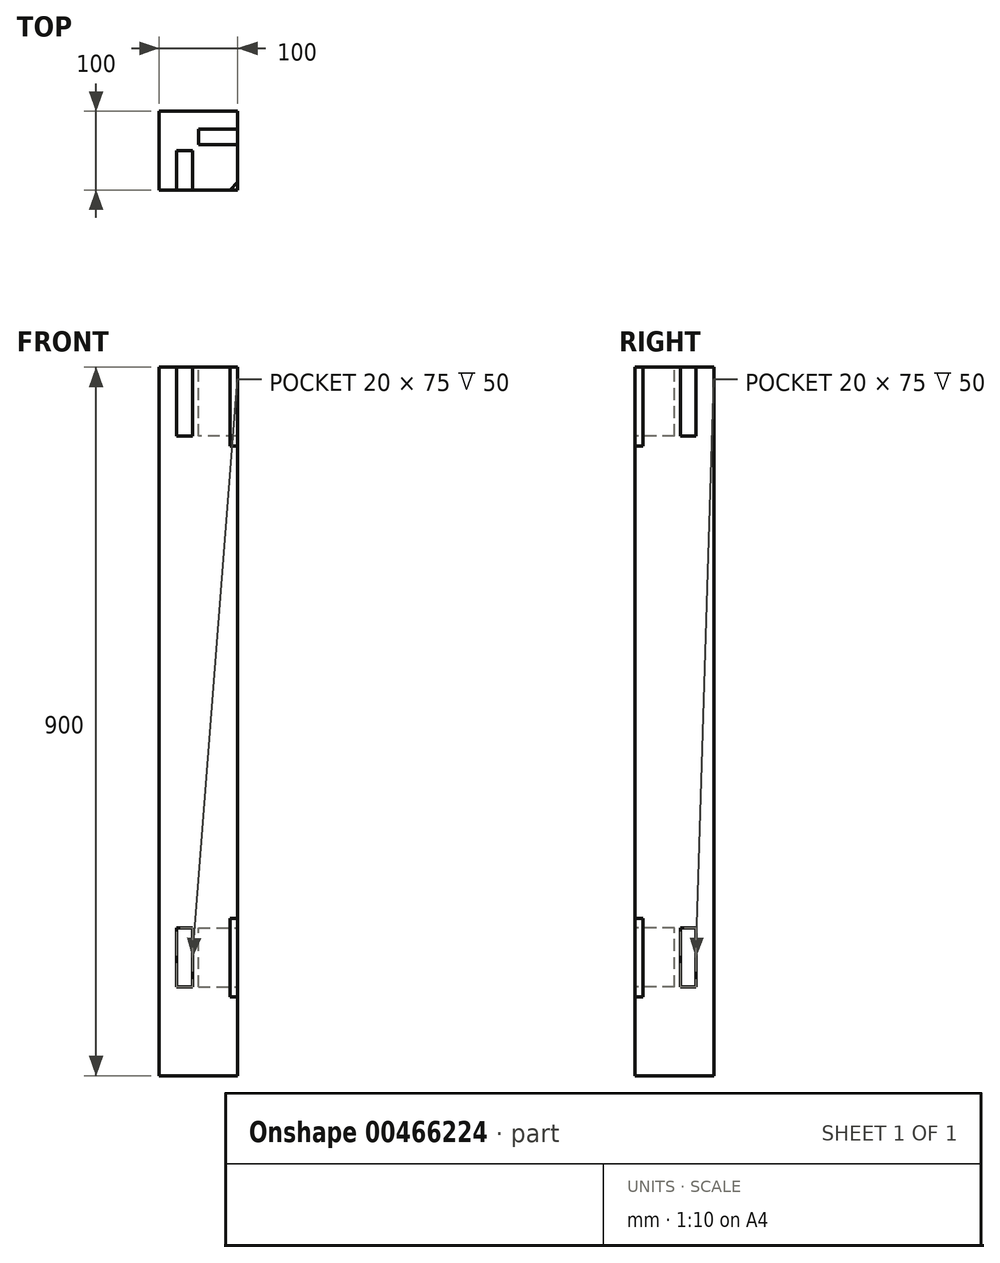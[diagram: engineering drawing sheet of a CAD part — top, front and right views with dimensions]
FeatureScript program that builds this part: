
annotation { "Feature Type Name" : "Feature", "Feature Type Description" : "" }
export const myFeature = defineFeature(function(context is Context, id is Id, definition is map)
    precondition{}
    {
        {
            assignVariable(context, id + "F0", {"name" : "thickness", "anyValue" : 100 * mm});
        }
        {
            var Q0;
            Q0=qCreatedBy(makeId("Top.planeOp"),FACE);
            var sketch = newSketch(context, id + "F1", { "sketchPlane" : qUnion([Q0])});
            skLineSegment(sketch, "E0.bottom", {"start": v(-50, 50) * mm, "end": v(50, 50) * mm});
            skLineSegment(sketch, "E0.top", {"start": v(-50, -50) * mm, "end": v(50, -50) * mm});
            skLineSegment(sketch, "E0.left", {"start": v(-50, 50) * mm, "end": v(-50, -50) * mm});
            skLineSegment(sketch, "E0.right", {"start": v(50, 50) * mm, "end": v(50, -50) * mm});
            skSolve(sketch);
        }
        {
            assignVariable(context, id + "F2", {"name" : "height", "anyValue" : 900 * mm});
        }
        {
            var Q0;
            Q0=makeQuery(id+"F1.imprint","IMPRINT",FACE,{"disambiguationData":[TD([[makeQuery(id+"F1.imprint","IMPRINT",EDGE,{"derivedFrom":sQuery(id+"F1.wireOp",EDGE,"E0.bottom")}),-1.0]])]});
            extrude(context, id + "F3", {"entities" : qUnion([Q0]), "depth" : getVariable(context, 'height')});
        }
        {
            var Q0;
            Q0=makeQuery(id+"F3.opExtrude","SWEPT_FACE",FACE,{"disambiguationData":[OSD([sQuery(id+"F1.wireOp",EDGE,"E0.right")])]});
            var sketch = newSketch(context, id + "F4", { "sketchPlane" : qUnion([Q0])});
            skLineSegment(sketch, "E1.bottom", {"start": v(27.5, 112.5) * mm, "end": v(7.5, 112.5) * mm});
            skLineSegment(sketch, "E1.top", {"start": v(27.5, 187.5) * mm, "end": v(7.5, 187.5) * mm});
            skLineSegment(sketch, "E1.left", {"start": v(27.5, 112.5) * mm, "end": v(27.5, 187.5) * mm});
            skLineSegment(sketch, "E1.right", {"start": v(7.5, 112.5) * mm, "end": v(7.5, 187.5) * mm});
            skPoint(sketch, "E1.middle", {"position": v(17.5, 150) * mm});
            skLineSegment(sketch, "E2.bottom", {"start": v(40, 200) * mm, "end": v(-5, 200) * mm, "construction": true});
            skLineSegment(sketch, "E2.top", {"start": v(40, 100) * mm, "end": v(-5, 100) * mm, "construction": true});
            skLineSegment(sketch, "E2.left", {"start": v(40, 200) * mm, "end": v(40, 100) * mm, "construction": true});
            skLineSegment(sketch, "E2.right", {"start": v(-5, 200) * mm, "end": v(-5, 100) * mm, "construction": true});
            skSolve(sketch);
        }
        {
            var Q0;
            Q0=makeQuery(id+"F4.imprint","IMPRINT",FACE,{"disambiguationData":[TD([[makeQuery(id+"F4.imprint","IMPRINT",EDGE,{"derivedFrom":sQuery(id+"F4.wireOp",EDGE,"E1.bottom")}),-1.0]])]});
            extrude(context, id + "F5", {"entities" : qUnion([Q0]), "operationType" : NewBodyOperationType.REMOVE, "oppositeDirection" : true, "depth" : getVariable(context, 'thickness') / 2});
        }
        {
            var Q0;
            Q0=makeQuery(id+"F3.opExtrude","SWEPT_FACE",FACE,{"disambiguationData":[OSD([sQuery(id+"F1.wireOp",EDGE,"E0.top")])]});
            var sketch = newSketch(context, id + "F6", { "sketchPlane" : qUnion([Q0])});
            skLineSegment(sketch, "E3.bottom", {"start": v(-7.5, 112.5) * mm, "end": v(-27.5, 112.5) * mm});
            skLineSegment(sketch, "E3.top", {"start": v(-7.5, 187.5) * mm, "end": v(-27.5, 187.5) * mm});
            skLineSegment(sketch, "E3.left", {"start": v(-7.5, 112.5) * mm, "end": v(-7.5, 187.5) * mm});
            skLineSegment(sketch, "E3.right", {"start": v(-27.5, 112.5) * mm, "end": v(-27.5, 187.5) * mm});
            skPoint(sketch, "E3.middle", {"position": v(-17.5, 150) * mm});
            skLineSegment(sketch, "E4.bottom", {"start": v(5, 200) * mm, "end": v(-40, 200) * mm, "construction": true});
            skLineSegment(sketch, "E4.top", {"start": v(5, 100) * mm, "end": v(-40, 100) * mm, "construction": true});
            skLineSegment(sketch, "E4.left", {"start": v(5, 200) * mm, "end": v(5, 100) * mm, "construction": true});
            skLineSegment(sketch, "E4.right", {"start": v(-40, 200) * mm, "end": v(-40, 100) * mm, "construction": true});
            skSolve(sketch);
        }
        {
            var Q0;
            Q0=makeQuery(id+"F6.imprint","IMPRINT",FACE,{"disambiguationData":[TD([[makeQuery(id+"F6.imprint","IMPRINT",EDGE,{"derivedFrom":sQuery(id+"F6.wireOp",EDGE,"E3.bottom")}),-1.0]])]});
            extrude(context, id + "F7", {"entities" : qUnion([Q0]), "operationType" : NewBodyOperationType.REMOVE, "oppositeDirection" : true, "depth" : getVariable(context, 'thickness') / 2});
        }
        {
            var Q0;
            Q0=qCreatedBy(makeId("Top.planeOp"),FACE);
            var sketch = newSketch(context, id + "F8", { "sketchPlane" : qUnion([Q0])});
            skLineSegment(sketch, "E5", {"start": v(40, -50) * mm, "end": v(50, -50) * mm});
            skLineSegment(sketch, "E6", {"start": v(50, -50) * mm, "end": v(50, -40) * mm});
            skLineSegment(sketch, "E7", {"start": v(50, -40) * mm, "end": v(40, -50) * mm});
            skSolve(sketch);
        }
        {
            var Q0;
            Q0 = qSketchRegion(id + "F8", true);
            extrude(context, id + "F9", {"entities" : qUnion([Q0]), "depth" : 100 * mm});
        }
        {
            var Q0;
            Q0=makeQuery(id+"F9.opExtrude","SWEPT_BODY",BODY,{"disambiguationData":[OSD([sQuery(id+"F8.wireOp",EDGE,"E5"),sQuery(id+"F8.wireOp",EDGE,"E6"),sQuery(id+"F8.wireOp",EDGE,"E7")])]});
            var Q1;
            Q1=makeQuery(id+"F3.opExtrude","SWEPT_EDGE",EDGE,{"disambiguationData":[OSD([sQuery(id+"F1.wireOp",EDGE,"E0.top"),sQuery(id+"F1.wireOp",EDGE,"E0.right")])]});
            var Q2;
            Q2=makeQuery(id+"F3.opExtrude","SWEPT_EDGE",EDGE,{"disambiguationData":[OSD([sQuery(id+"F1.wireOp",EDGE,"E0.top"),sQuery(id+"F1.wireOp",EDGE,"E0.right")])]});
            transform(context, id + "F10", {"entities" : qUnion([Q0]), "transformType" : TransformType.TRANSLATION_DISTANCE, "transformDirection" : qUnion([Q2]), "distance" : getVariable(context, 'thickness'), "oppositeDirection" : true, "makeCopy" : false});
        }
        {
            var Q0;
            Q0=makeQuery(id+"F9.opExtrude","SWEPT_BODY",BODY,{"disambiguationData":[OSD([sQuery(id+"F8.wireOp",EDGE,"E5"),sQuery(id+"F8.wireOp",EDGE,"E6"),sQuery(id+"F8.wireOp",EDGE,"E7")])]});
            var Q1;
            Q1=makeQuery(id+"F3.opExtrude","SWEPT_BODY",BODY,{"disambiguationData":[OSD([sQuery(id+"F1.wireOp",EDGE,"E0.bottom"),sQuery(id+"F1.wireOp",EDGE,"E0.top"),sQuery(id+"F1.wireOp",EDGE,"E0.left"),sQuery(id+"F1.wireOp",EDGE,"E0.right")])]});
            booleanBodies(context, id + "F11", {"operationType" : BooleanOperationType.SUBTRACTION, "tools" : qUnion([Q0]), "targets" : qUnion([Q1])});
        }
        {
            var Q0;
            Q0=makeQuery(id+"F3.opExtrude","CAP_FACE",FACE,{"disambiguationData":[OSD([sQuery(id+"F1.wireOp",EDGE,"E0.bottom"),sQuery(id+"F1.wireOp",EDGE,"E0.top"),sQuery(id+"F1.wireOp",EDGE,"E0.left"),sQuery(id+"F1.wireOp",EDGE,"E0.right")])],"isStart":false});
            var sketch = newSketch(context, id + "F12", { "sketchPlane" : qUnion([Q0])});
            skLineSegment(sketch, "E8", {"start": v(50, -40) * mm, "end": v(40, -50) * mm});
            skLineSegment(sketch, "E9", {"start": v(40, -50) * mm, "end": v(50, -50) * mm});
            skLineSegment(sketch, "E10", {"start": v(50, -50) * mm, "end": v(50, -40) * mm});
            skLineSegment(sketch, "E11", {"start": v(50, 27.5) * mm, "end": v(0, 27.5) * mm});
            skLineSegment(sketch, "E12", {"start": v(0, 7.5) * mm, "end": v(50, 7.5) * mm});
            skLineSegment(sketch, "E13", {"start": v(50, -50) * mm, "end": v(-50, 50) * mm, "construction": true});
            skLineSegment(sketch, "E14", {"start": v(-7.5, 0) * mm, "end": v(-7.5, -50) * mm});
            skLineSegment(sketch, "E15", {"start": v(-27.5, 0) * mm, "end": v(-27.5, -50) * mm});
            skLineSegment(sketch, "E16", {"start": v(0, 27.5) * mm, "end": v(0, 7.5) * mm});
            skLineSegment(sketch, "E17", {"start": v(-27.5, 0) * mm, "end": v(-7.5, 0) * mm});
            skSolve(sketch);
        }
        {
            var Q0;
            {var subQ3=sQuery(id+"F12.wireOp",EDGE,"E11");Q0=makeQuery(id+"F12.imprint","IMPRINT",FACE,{"disambiguationData":[TD([[makeQuery(id+"F12.imprint","IMPRINT",EDGE,{"derivedFrom":subQ3}),1.0]])]});}
            var Q1;
            {var subQ0=sQuery(id+"F12.wireOp",EDGE,"E14");Q1=makeQuery(id+"F12.imprint","IMPRINT",FACE,{"disambiguationData":[TD([[makeQuery(id+"F12.imprint","IMPRINT",EDGE,{"derivedFrom":subQ0}),-1.0]])]});}
            extrude(context, id + "F13", {"entities" : qUnion([Q0, Q1]), "operationType" : NewBodyOperationType.REMOVE, "oppositeDirection" : true, "depth" : 87.5 * mm});
        }
        {
            var Q0;
            Q0=makeQuery(id+"F4.imprint","IMPRINT",FACE,{"disambiguationData":[TD([[makeQuery(id+"F4.imprint","IMPRINT",EDGE,{"derivedFrom":sQuery(id+"F4.wireOp",EDGE,"E1.bottom")}),1.0]])]});
            var sketch = newSketch(context, id + "F14", { "sketchPlane" : qUnion([Q0])});
            skLineSegment(sketch, "E18", {"start": v(40, 900) * mm, "end": v(40, 800) * mm, "construction": true});
            skLineSegment(sketch, "E19", {"start": v(40, 800) * mm, "end": v(-5, 800) * mm, "construction": true});
            skLineSegment(sketch, "E20", {"start": v(-5, 800) * mm, "end": v(-5, 900) * mm, "construction": true});
            skSolve(sketch);
        }
        {
            var Q0;
            Q0=makeQuery(id+"F12.imprint","IMPRINT",FACE,{"disambiguationData":[TD([[makeQuery(id+"F12.imprint","IMPRINT",EDGE,{"derivedFrom":sQuery(id+"F12.wireOp",EDGE,"E8")}),1.0]])]});
            var Q1;
            Q1=sQuery(id+"F12.wireOp",EDGE,"E8");
            extrude(context, id + "F15", {"entities" : qUnion([Q0]), "operationType" : NewBodyOperationType.REMOVE, "surfaceEntities" : qUnion([Q1]), "oppositeDirection" : true, "depth" : 100 * mm});
        }
    });
